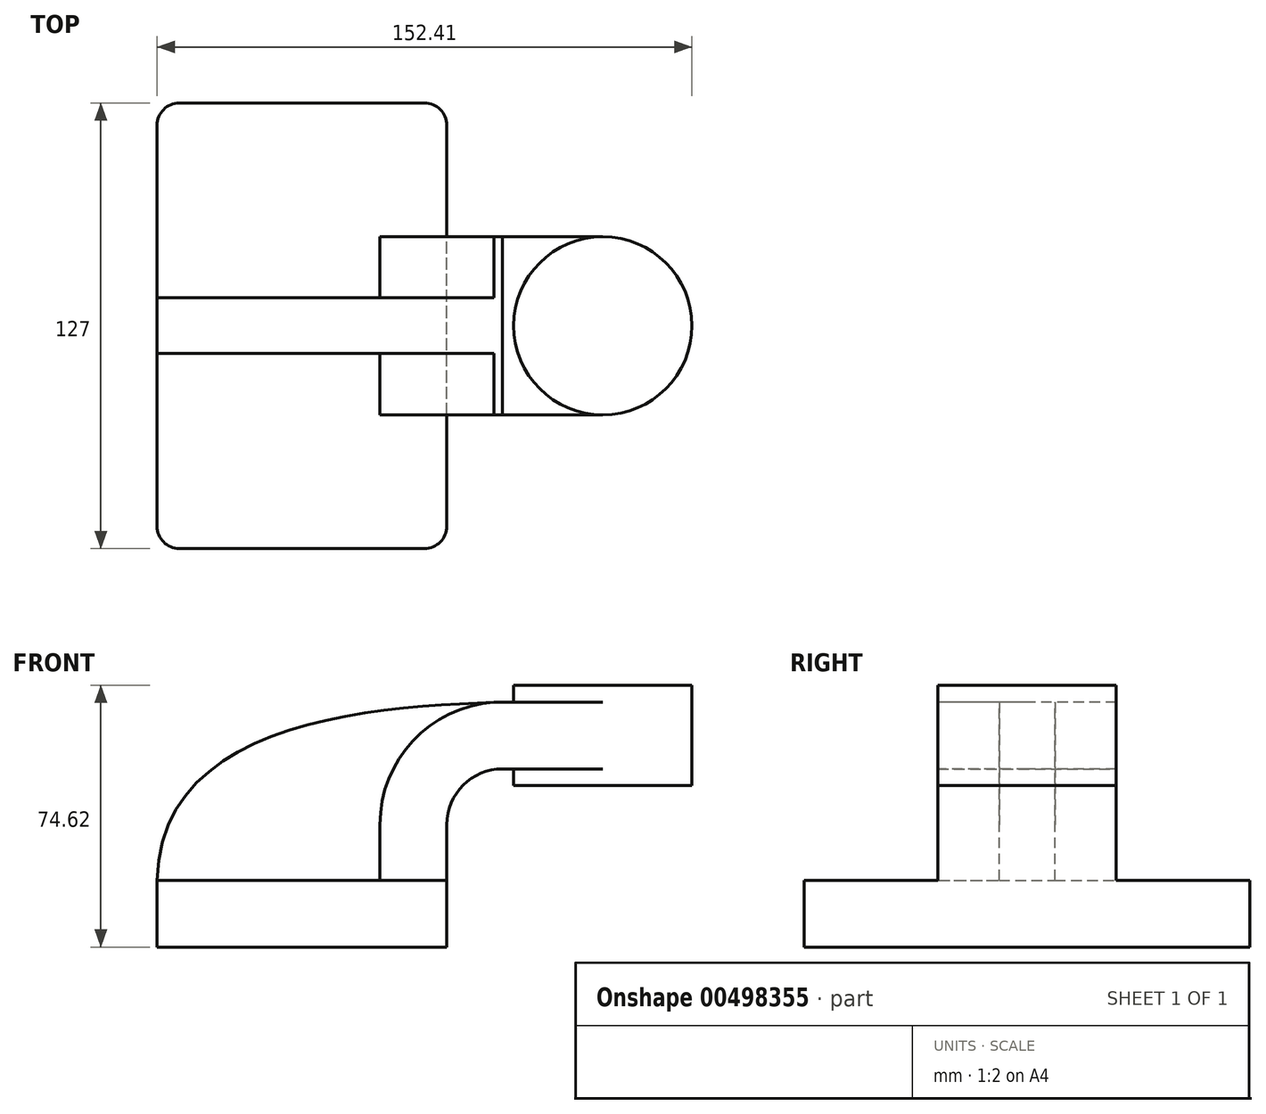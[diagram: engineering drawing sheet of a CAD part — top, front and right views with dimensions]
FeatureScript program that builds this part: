
annotation { "Feature Type Name" : "Feature", "Feature Type Description" : "" }
export const myFeature = defineFeature(function(context is Context, id is Id, definition is map)
    precondition{}
    {
        {
            var Q0;
            Q0=qCreatedBy(makeId("Front.planeOp"),FACE);
            var sketch = newSketch(context, id + "F0", { "sketchPlane" : qUnion([Q0])});
            skLineSegment(sketch, "E0.bottom", {"start": v(-41.28, 9.52) * mm, "end": v(41.27, 9.53) * mm});
            skLineSegment(sketch, "E0.top", {"start": v(-41.28, -9.53) * mm, "end": v(41.28, -9.53) * mm});
            skLineSegment(sketch, "E0.left", {"start": v(-41.28, 9.52) * mm, "end": v(-41.27, -9.53) * mm});
            skLineSegment(sketch, "E0.right", {"start": v(41.28, 9.53) * mm, "end": v(41.28, -9.52) * mm});
            skPoint(sketch, "E0.middle", {"position": v(0, 0) * mm});
            skLineSegment(sketch, "E1.bottom", {"start": v(60.33, 65.09) * mm, "end": v(111.13, 65.09) * mm});
            skLineSegment(sketch, "E1.top", {"start": v(60.33, 36.51) * mm, "end": v(111.13, 36.51) * mm});
            skLineSegment(sketch, "E1.left", {"start": v(60.33, 65.09) * mm, "end": v(60.33, 36.51) * mm});
            skLineSegment(sketch, "E1.right", {"start": v(111.13, 65.09) * mm, "end": v(111.13, 36.51) * mm});
            skPoint(sketch, "E1.middle", {"position": v(85.73, 50.8) * mm});
            skLineSegment(sketch, "E2", {"start": v(41.27, 9.53) * mm, "end": v(41.27, 25.4) * mm});
            skArc(sketch, "E3", {"start": v(41.27, 25.4) * mm, "mid": v(45.92, 36.63) * mm, "end": v(57.15, 41.27) * mm});
            skLineSegment(sketch, "E4", {"start": v(57.15, 41.28) * mm, "end": v(85.73, 41.28) * mm});
            skLineSegment(sketch, "E5.0", {"start": v(57.15, 60.33) * mm, "end": v(85.73, 60.33) * mm});
            skArc(sketch, "E5.1", {"start": v(22.23, 25.4) * mm, "mid": v(32.45, 50.1) * mm, "end": v(57.15, 60.32) * mm});
            skLineSegment(sketch, "E5.2", {"start": v(22.22, 9.53) * mm, "end": v(22.22, 25.4) * mm});
            skLineSegment(sketch, "E6", {"start": v(85.73, 41.28) * mm, "end": v(85.73, 60.33) * mm});
            skFitSpline(sketch, "E7", {"points": [v(-41.28, 9.52) * mm, v(57.15, 60.33) * mm], "startDerivative": vector(2.96, 138.9) * mm, "endDerivative": vector(106.43, 3.57) * mm});
            skLineSegment(sketch, "E8", {"start": v(85.73, 41.28) * mm, "end": v(85.73, 36.51) * mm});
            skLineSegment(sketch, "E9", {"start": v(85.73, 60.33) * mm, "end": v(85.73, 65.09) * mm});
            skSolve(sketch);
        }
        {
            var Q0;
            Q0=makeQuery(id+"F0.imprint","IMPRINT",FACE,{"disambiguationData":[TD([[makeQuery(id+"F0.imprint","IMPRINT",EDGE,{"derivedFrom":sQuery(id+"F0.wireOp",EDGE,"E0.top")}),1.0]])]});
            extrude(context, id + "F1", {"entities" : qUnion([Q0]), "endBound" : BoundingType.SYMMETRIC, "depth" : 127 * mm});
        }
        {
            var Q0;
            {var subQ1=sQuery(id+"F0.wireOp",EDGE,"E2");Q0=makeQuery(id+"F0.imprint","IMPRINT",FACE,{"disambiguationData":[TD([[makeQuery(id+"F0.imprint","IMPRINT",EDGE,{"derivedFrom":subQ1}),1.0]])]});}
            var Q1;
            {var subQ5=sQuery(id+"F0.wireOp",EDGE,"E6");Q1=makeQuery(id+"F0.imprint","IMPRINT",FACE,{"disambiguationData":[TD([[makeQuery(id+"F0.imprint","IMPRINT",EDGE,{"derivedFrom":subQ5}),1.0]])]});}
            extrude(context, id + "F2", {"entities" : qUnion([Q0, Q1]), "operationType" : NewBodyOperationType.ADD, "endBound" : BoundingType.SYMMETRIC, "depth" : 50.8 * mm});
        }
        {
            var Q0;
            {var subQ3=sQuery(id+"F0.wireOp",EDGE,"E5.2");Q0=makeQuery(id+"F0.imprint","IMPRINT",FACE,{"disambiguationData":[TD([[makeQuery(id+"F0.imprint","IMPRINT",EDGE,{"derivedFrom":subQ3}),1.0]])]});}
            extrude(context, id + "F3", {"entities" : qUnion([Q0]), "operationType" : NewBodyOperationType.ADD, "endBound" : BoundingType.SYMMETRIC, "depth" : 15.88 * mm});
        }
        {
            var Q0;
            {var subQ0=sQuery(id+"F0.wireOp",EDGE,"E1.right");Q0=makeQuery(id+"F0.imprint","IMPRINT",FACE,{"disambiguationData":[TD([[makeQuery(id+"F0.imprint","IMPRINT",EDGE,{"derivedFrom":subQ0}),-1.0]])]});}
            var Q1;
            Q1=sQuery(id+"F0.wireOp",EDGE,"E6");
            revolve(context, id + "F4", {"operationType" : NewBodyOperationType.ADD, "entities" : qUnion([Q0]), "axis" : qUnion([Q1]), "revolveType" : RevolveType.FULL});
        }
        {
            var Q0;
            Q0=makeQuery(id+"F1.opExtrude","CAP_EDGE",EDGE,{"disambiguationData":[OSD([sQuery(id+"F0.wireOp",EDGE,"E0.right")])],"isStart":true});
            var Q1;
            Q1=makeQuery(id+"F1.opExtrude","CAP_EDGE",EDGE,{"disambiguationData":[OSD([sQuery(id+"F0.wireOp",EDGE,"E0.left")])],"isStart":true});
            var Q2;
            Q2=makeQuery(id+"F1.opExtrude","CAP_EDGE",EDGE,{"disambiguationData":[OSD([sQuery(id+"F0.wireOp",EDGE,"E0.left")])],"isStart":false});
            var Q3;
            Q3=makeQuery(id+"F1.opExtrude","CAP_EDGE",EDGE,{"disambiguationData":[OSD([sQuery(id+"F0.wireOp",EDGE,"E0.right")])],"isStart":false});
            fillet(context, id + "F5", {"entities" : qUnion([Q0, Q1, Q2, Q3]), "radius" : 6.35 * mm, "tangentPropagation" : true, "allowEdgeOverflow" : false});
        }
    });
